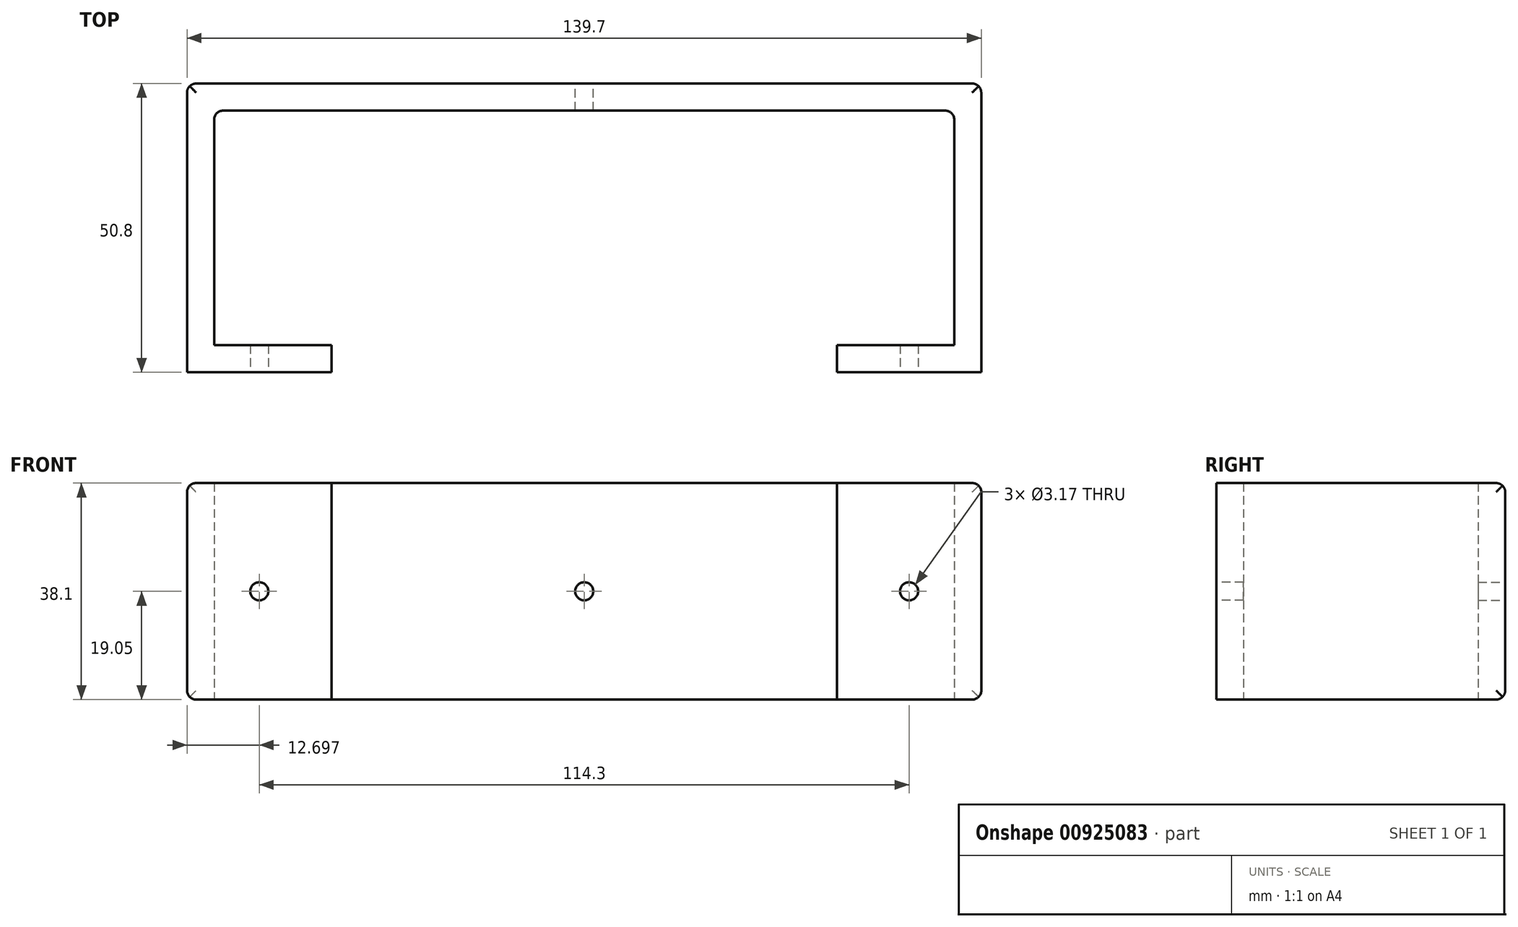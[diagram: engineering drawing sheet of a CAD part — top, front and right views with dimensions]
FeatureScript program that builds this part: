
annotation { "Feature Type Name" : "Feature", "Feature Type Description" : "" }
export const myFeature = defineFeature(function(context is Context, id is Id, definition is map)
    precondition{}
    {
        {
            var Q0;
            Q0=qCreatedBy(makeId("Top.planeOp"),FACE);
            var sketch = newSketch(context, id + "F0", { "sketchPlane" : qUnion([Q0])});
            skLineSegment(sketch, "E0", {"start": v(-44.46, -25.4) * mm, "end": v(-69.86, -25.4) * mm});
            skLineSegment(sketch, "E1", {"start": v(-69.86, -25.4) * mm, "end": v(-69.86, 23.8) * mm});
            skLineSegment(sketch, "E2", {"start": v(-68.26, 25.4) * mm, "end": v(68.24, 25.4) * mm});
            skLineSegment(sketch, "E3", {"start": v(69.84, 23.8) * mm, "end": v(69.84, -25.4) * mm});
            skLineSegment(sketch, "E4", {"start": v(69.84, -25.4) * mm, "end": v(44.44, -25.4) * mm});
            skLineSegment(sketch, "E5", {"start": v(44.44, -25.4) * mm, "end": v(44.44, -20.64) * mm});
            skLineSegment(sketch, "E6", {"start": v(44.44, -20.64) * mm, "end": v(65.07, -20.64) * mm});
            skLineSegment(sketch, "E7", {"start": v(65.07, -20.64) * mm, "end": v(65.07, 19.04) * mm});
            skLineSegment(sketch, "E8", {"start": v(63.47, 20.64) * mm, "end": v(-63.5, 20.64) * mm});
            skLineSegment(sketch, "E9", {"start": v(-65.1, 19.04) * mm, "end": v(-65.1, -20.64) * mm});
            skLineSegment(sketch, "E10", {"start": v(-65.1, -20.64) * mm, "end": v(-44.45, -20.64) * mm});
            skLineSegment(sketch, "E11", {"start": v(-44.45, -20.64) * mm, "end": v(-44.46, -25.4) * mm});
            skPoint(sketch, "E12.visualSharp", {"position": v(-69.86, 25.4) * mm});
            skArc(sketch, "E12.filletArc", {"start": v(-68.26, 25.4) * mm, "mid": v(-69.4, 24.93) * mm, "end": v(-69.86, 23.8) * mm});
            skPoint(sketch, "E13.visualSharp", {"position": v(69.84, 25.4) * mm});
            skArc(sketch, "E13.filletArc", {"start": v(69.84, 23.8) * mm, "mid": v(69.37, 24.93) * mm, "end": v(68.24, 25.4) * mm});
            skPoint(sketch, "E14.visualSharp", {"position": v(-65.1, 20.64) * mm});
            skArc(sketch, "E14.filletArc", {"start": v(-63.5, 20.64) * mm, "mid": v(-64.63, 20.17) * mm, "end": v(-65.1, 19.04) * mm});
            skPoint(sketch, "E15.visualSharp", {"position": v(65.07, 20.64) * mm});
            skArc(sketch, "E15.filletArc", {"start": v(65.07, 19.04) * mm, "mid": v(64.6, 20.17) * mm, "end": v(63.47, 20.64) * mm});
            skSolve(sketch);
        }
        {
            var Q0;
            Q0=qSketchRegion(id+"F0",true);
            extrude(context, id + "F1", {"entities" : qUnion([Q0]), "depth" : 38.1 * mm, "offsetDistance" : 25.4 * mm});
        }
        {
            var Q0;
            Q0=makeQuery(id+"F1.opExtrude","SWEPT_FACE",FACE,{"disambiguationData":[OSD([sQuery(id+"F0.wireOp",EDGE,"E0")])]});
            var sketch = newSketch(context, id + "F2", { "sketchPlane" : qUnion([Q0])});
            skCircle(sketch, "E16", {"center": v(-57.16, 19.05) * mm, "radius": 1.59 * mm});
            skCircle(sketch, "E17", {"center": v(57.14, 19.05) * mm, "radius": 1.59 * mm});
            skSolve(sketch);
        }
        {
            var Q0;
            Q0=qSketchRegion(id+"F2",true);
            extrude(context, id + "F3", {"entities" : qUnion([Q0]), "operationType" : NewBodyOperationType.REMOVE, "oppositeDirection" : true, "depth" : 4.76 * mm, "offsetDistance" : 25.4 * mm});
        }
        {
            var Q0;
            Q0=makeQuery(id+"F1.opExtrude","SWEPT_FACE",FACE,{"disambiguationData":[OSD([sQuery(id+"F0.wireOp",EDGE,"E2")])]});
            var sketch = newSketch(context, id + "F4", { "sketchPlane" : qUnion([Q0])});
            skCircle(sketch, "E18", {"center": v(0, 19.05) * mm, "radius": 1.59 * mm});
            skSolve(sketch);
        }
        {
            var Q0;
            Q0=qSketchRegion(id+"F4",true);
            extrude(context, id + "F5", {"entities" : qUnion([Q0]), "operationType" : NewBodyOperationType.REMOVE, "oppositeDirection" : true, "depth" : 4.76 * mm, "offsetDistance" : 25.4 * mm});
        }
        {
            var Q0;
            Q0=makeQuery(id+"F1.opExtrude","SWEPT_FACE",FACE,{"disambiguationData":[OSD([sQuery(id+"F0.wireOp",EDGE,"E2")])]});
            var sketch = newSketch(context, id + "F6", { "sketchPlane" : qUnion([Q0])});
            skLineSegment(sketch, "E19", {"start": v(-68.24, 38.1) * mm, "end": v(-68.24, 38.1) * mm});
            skLineSegment(sketch, "E20", {"start": v(-69.84, 36.5) * mm, "end": v(-69.84, 36.5) * mm});
            skPoint(sketch, "E21.visualSharp", {"position": v(-69.84, 38.1) * mm});
            skArc(sketch, "E21.filletArc", {"start": v(-68.24, 38.1) * mm, "mid": v(-69.37, 37.63) * mm, "end": v(-69.84, 36.5) * mm});
            skLineSegment(sketch, "E22", {"start": v(-68.24, 0) * mm, "end": v(-68.24, 0) * mm});
            skLineSegment(sketch, "E23", {"start": v(-69.84, 1.6) * mm, "end": v(-69.84, 1.6) * mm});
            skPoint(sketch, "E24.visualSharp", {"position": v(-69.84, 0) * mm});
            skArc(sketch, "E24.filletArc", {"start": v(-69.84, 1.6) * mm, "mid": v(-69.37, 0.47) * mm, "end": v(-68.24, 0) * mm});
            skLineSegment(sketch, "E25", {"start": v(68.26, 0) * mm, "end": v(68.26, 0) * mm});
            skLineSegment(sketch, "E26", {"start": v(69.86, 1.6) * mm, "end": v(69.86, 1.6) * mm});
            skPoint(sketch, "E27.visualSharp", {"position": v(69.86, 0) * mm});
            skArc(sketch, "E27.filletArc", {"start": v(68.26, 0) * mm, "mid": v(69.4, 0.47) * mm, "end": v(69.86, 1.6) * mm});
            skLineSegment(sketch, "E28", {"start": v(68.26, 38.1) * mm, "end": v(68.26, 38.1) * mm});
            skLineSegment(sketch, "E29", {"start": v(69.86, 36.5) * mm, "end": v(69.86, 36.5) * mm});
            skPoint(sketch, "E30.visualSharp", {"position": v(69.86, 38.1) * mm});
            skArc(sketch, "E30.filletArc", {"start": v(69.86, 36.5) * mm, "mid": v(69.4, 37.63) * mm, "end": v(68.26, 38.1) * mm});
            skLineSegment(sketch, "E31", {"start": v(68.26, 38.1) * mm, "end": v(69.86, 38.1) * mm});
            skLineSegment(sketch, "E32", {"start": v(69.86, 38.1) * mm, "end": v(69.86, 36.5) * mm});
            skLineSegment(sketch, "E33", {"start": v(69.86, 1.6) * mm, "end": v(69.86, 0) * mm});
            skLineSegment(sketch, "E34", {"start": v(69.86, 0) * mm, "end": v(68.26, 0) * mm});
            skLineSegment(sketch, "E35", {"start": v(-69.84, 38.1) * mm, "end": v(-69.84, 36.5) * mm});
            skLineSegment(sketch, "E36", {"start": v(-69.84, 38.1) * mm, "end": v(-68.24, 38.1) * mm});
            skLineSegment(sketch, "E37", {"start": v(-69.84, 1.6) * mm, "end": v(-69.84, 0) * mm});
            skLineSegment(sketch, "E38", {"start": v(-68.24, 0) * mm, "end": v(-69.84, 0) * mm});
            skSolve(sketch);
        }
        {
            var Q0;
            Q0=qSketchRegion(id+"F6",true);
            extrude(context, id + "F7", {"entities" : qUnion([Q0]), "operationType" : NewBodyOperationType.REMOVE, "oppositeDirection" : true, "depth" : 50.8 * mm, "offsetDistance" : 25.4 * mm});
        }
        {
            var Q0;
            Q0=makeQuery(id+"F1.opExtrude","SWEPT_FACE",FACE,{"disambiguationData":[OSD([sQuery(id+"F0.wireOp",EDGE,"E3")])]});
            var sketch = newSketch(context, id + "F8", { "sketchPlane" : qUnion([Q0])});
            skLineSegment(sketch, "E39", {"start": v(23.8, 38.1) * mm, "end": v(23.8, 38.1) * mm});
            skLineSegment(sketch, "E40", {"start": v(25.4, 36.5) * mm, "end": v(25.4, 36.5) * mm});
            skPoint(sketch, "E41.visualSharp", {"position": v(25.4, 38.1) * mm});
            skArc(sketch, "E41.filletArc", {"start": v(25.4, 36.5) * mm, "mid": v(24.93, 37.63) * mm, "end": v(23.8, 38.1) * mm});
            skLineSegment(sketch, "E42", {"start": v(23.8, 0) * mm, "end": v(23.8, 0) * mm});
            skLineSegment(sketch, "E43", {"start": v(25.4, 1.6) * mm, "end": v(25.4, 1.6) * mm});
            skPoint(sketch, "E44.visualSharp", {"position": v(25.4, 0) * mm});
            skArc(sketch, "E44.filletArc", {"start": v(23.8, 0) * mm, "mid": v(24.93, 0.47) * mm, "end": v(25.4, 1.6) * mm});
            skLineSegment(sketch, "E45", {"start": v(25.4, 1.6) * mm, "end": v(25.4, 0) * mm});
            skLineSegment(sketch, "E46", {"start": v(25.4, 0) * mm, "end": v(23.8, 0) * mm});
            skLineSegment(sketch, "E47", {"start": v(23.8, 38.1) * mm, "end": v(25.4, 38.1) * mm});
            skLineSegment(sketch, "E48", {"start": v(25.4, 36.5) * mm, "end": v(25.4, 38.1) * mm});
            skSolve(sketch);
        }
        {
            var Q0;
            Q0=qSketchRegion(id+"F8",true);
            extrude(context, id + "F9", {"entities" : qUnion([Q0]), "operationType" : NewBodyOperationType.REMOVE, "oppositeDirection" : true, "depth" : 139.7 * mm, "offsetDistance" : 25.4 * mm});
        }
    });
